# Revit family: URA SPOT Autotest - Permanent_Non Permanent_Color
name_source: partatom
category: Luminaires
units: mm (PartAtom-declared; Revit-internal decimal feet)

## family parameters
Cote de connecteur circulaire = Utiliser le diamètre
Couper avec des vides une fois chargée = Non
Hôte = Face
Partagée = Non
Repere pour localisation dans la piece = Non
Source d'éclairage = Non
Type d'élément = Normal

## types (5) — shared parameters
Color = Black
Connected Object = Non
Connection type = Screw connection
Diameter = 125 mm
Elévation par défaut = 2300 mm
Emergency power supply = Autonomous (individual battery)
Fabricant = LEGRAND
Frequency = 50-60
Function = Escape and mood lighting
General Conditions of Use = https://export.legrand.com
Height = 45 mm
IK = 07
IP = 42
Installation method = Flush-mounting
Material = Plastic
Operating temperature MIN-MAX = -5-35
Pictogram type = other
Power supply = 230 AC/DC
Protection class = II
Recessed height = 42 mm
Standby consumption = 0.0 mA
System power = 2 W
URL = https://www.legrand.com
battery status = NiMh
light source = LED not exchangeable
terminal capacity = 1,5-2,5

## per-type parameters (varying)
| type | Autonomy | Control system | Product designation | Reference | Spare battery | Switching type | Useful luminous flux |
| 100LM-1H Color | 1H | Autotest Automatic | EMERGENCY LIGHT U22ROUND FLUSH PERMANENT - NON PERM 100 LUMENS 1H AUTOTEST COLOR | LG-660142BK | 660182 | Permanent | 100 lm |
| 200LM-1H Color | 1H | Autotest Automatic | EMERGENCY LIGHT U22ROUND FLUSH PERMANENT - NON PERM 200 LUMENS 1H AUTOTEST COLOR | LG-660144BK | 660182 | Permanent | 200 lm |
| 350LM-1H Color | 1H | Autotest Automatic | EMERGENCY LIGHT U22ROUND FLUSH PERMANENT - NON PERM 350 LUMENS 1H AUTOTEST COLOR | LG-660145BK | 660184 | Permanent | 350 lm |
| 100LM-3H Color | 3H | without | EMERGENCY LIGHT U22ROUNDPERMANENT  NON PERMANENT 100 LUMENS 3H AUTOTEST COLOR | LG-660146BK | 660182 | Non permanent | 100 lm |
| 200LM-2H Color | 2H | Autotest Automatic | EMERGENCY LIGHT U22ROUND FLUSH PERMANENT - NON PERM 200 LUMENS 2H AUTOTEST COLOR | LG-660147BK | 660184 | Permanent | 200 lm |
